# Revit family: Sanitary_Taps-Mixers_hansgrohe_29233XXX-hansgrohe-Bidette-hand-shower-1_000
name_source: partatom
category: Plumbing Fixtures
units: mm (PartAtom-declared; Revit-internal decimal feet)

## family parameters
Always vertical = No
Cut with Voids When Loaded = No
OmniClass Number = 23.31.11.00
OmniClass Title = Faucets
Part Type = Normal
Room Calculation Point = No
Round Connector Dimension = Use Diameter
Shared = No
Work Plane-Based = Yes

## types (6) — shared parameters
Default Elevation = 48"
Description = Hansgrohe Bidette hand shower 1jet E EcoSmart+ for warm water with shower holder and shower hose 125 cm
Manufacturer = Hansgrohe
Model = 29233XXX
Product Guid = fc5cd1f5-cd69-4752-8296-04a9b9c1cbe8
Product Page URL = https://www.hansgrohe.com
Product data url = https://bimobject.com
URL = https://www.hansgrohe.com
Version = 1

## per-type parameters (varying)
| type | Material |
| 000 Chrome | Hansgrohe - Metal - 000 Chrome |
| 140 Brushed Bronze | Hansgrohe - Metal - 140 Brushed Bronze |
| 340 Brushed Black Chrome | Hansgrohe - Metal - 340 Brushed Black Chrome |
| 670 Matte Black | Hansgrohe - Metal - 670 Matte Black |
| 700 Matt White | Hansgrohe - Metal - 700 Matte White |
| 990 Polished Gold Optic | Hansgrohe - Metal - 990 Polished Gold Optic |

## geometry (parser evidence)
native form markers: Sweep x1
no freeform markers — native parametric forms only
